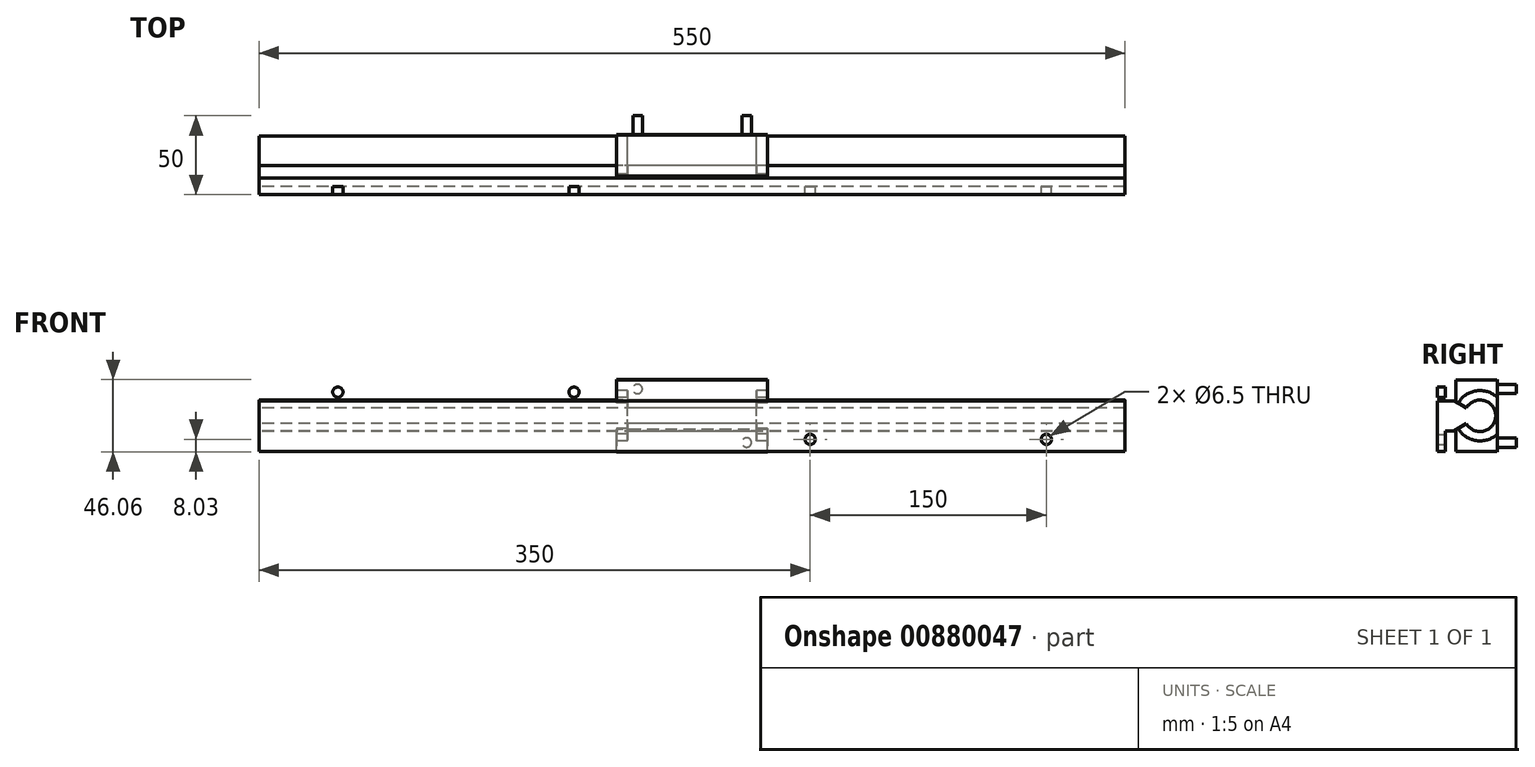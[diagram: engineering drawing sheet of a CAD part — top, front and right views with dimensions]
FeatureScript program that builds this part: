
annotation { "Feature Type Name" : "Feature", "Feature Type Description" : "" }
export const myFeature = defineFeature(function(context is Context, id is Id, definition is map)
    precondition{}
    {
        {
            var Q0;
            Q0=qCreatedBy(makeId("Right.planeOp"),FACE);
            var sketch = newSketch(context, id + "F0", { "sketchPlane" : qUnion([Q0])});
            skLineSegment(sketch, "E0", {"start": v(23, 0) * mm, "end": v(23, -24.18) * mm});
            skLineSegment(sketch, "E1", {"start": v(23, -24.18) * mm, "end": v(12, -24.18) * mm});
            skLineSegment(sketch, "E2", {"start": v(12, -24.18) * mm, "end": v(10.8, -22.8) * mm});
            skLineSegment(sketch, "E3", {"start": v(10.8, -22.8) * mm, "end": v(-15.2, -22.8) * mm});
            skLineSegment(sketch, "E4", {"start": v(-15.2, -22.8) * mm, "end": v(-15.2, -8.78) * mm});
            skArc(sketch, "E5", {"start": v(-8.66, -5) * mm, "mid": v(2.59, -9.66) * mm, "end": v(10, 0) * mm});
            skArc(sketch, "E6.0", {"start": v(-13.86, -8) * mm, "mid": v(4.14, -15.45) * mm, "end": v(16, 0) * mm});
            skLineSegment(sketch, "E7", {"start": v(-8.66, -5) * mm, "end": v(-16.54, -9.55) * mm});
            skPoint(sketch, "E8.orphan", {"position": v(-5, 0) * mm});
            skPoint(sketch, "E9.orphan", {"position": v(-16, 0) * mm});
            skPoint(sketch, "E10.MirrorP", {"position": v(-8, 0) * mm});
            skPoint(sketch, "E11.orphan", {"position": v(-27, 0) * mm});
            skLineSegment(sketch, "E12.top", {"start": v(-27, -22.6) * mm, "end": v(-22, -22.6) * mm});
            skLineSegment(sketch, "E12.left", {"start": v(-27, 0) * mm, "end": v(-27, -22.6) * mm});
            skLineSegment(sketch, "E12.right", {"start": v(-22, -12.7) * mm, "end": v(-22, -22.6) * mm});
            skLineSegment(sketch, "E13.MirrorCS", {"start": v(12, 24.18) * mm, "end": v(10.8, 22.8) * mm});
            skLineSegment(sketch, "E14.MirrorCS", {"start": v(-15.2, 22.8) * mm, "end": v(-15.2, 8.78) * mm});
            skLineSegment(sketch, "E15.MirrorCS", {"start": v(-27, 22.6) * mm, "end": v(-22, 22.6) * mm});
            skLineSegment(sketch, "E16.MirrorCS", {"start": v(-22, 12.7) * mm, "end": v(-22, 22.6) * mm});
            skLineSegment(sketch, "E17.MirrorCS", {"start": v(23, 24.18) * mm, "end": v(12, 24.18) * mm});
            skLineSegment(sketch, "E18.MirrorCS", {"start": v(-8.66, 5) * mm, "end": v(-16.54, 9.55) * mm});
            skLineSegment(sketch, "E19.MirrorCS", {"start": v(10.8, 22.8) * mm, "end": v(-15.2, 22.8) * mm});
            skArc(sketch, "E20.MirrorCS", {"start": v(-13.86, 8) * mm, "mid": v(4.14, 15.45) * mm, "end": v(16, 0) * mm});
            skLineSegment(sketch, "E21.MirrorCS", {"start": v(23, 0) * mm, "end": v(23, 24.18) * mm});
            skLineSegment(sketch, "E22.MirrorCS", {"start": v(-27, 0) * mm, "end": v(-27, 22.6) * mm});
            skArc(sketch, "E23.MirrorCS", {"start": v(-8.66, 5) * mm, "mid": v(2.59, 9.66) * mm, "end": v(10, 0) * mm});
            skLineSegment(sketch, "E24", {"start": v(-16.54, -9.55) * mm, "end": v(-22, -9.55) * mm});
            skLineSegment(sketch, "E25", {"start": v(-22, -12.7) * mm, "end": v(-22, -9.55) * mm});
            skLineSegment(sketch, "E26.MirrorCS", {"start": v(-16.54, 9.55) * mm, "end": v(-22, 9.55) * mm});
            skLineSegment(sketch, "E27.MirrorCS", {"start": v(-22, 12.7) * mm, "end": v(-22, 9.55) * mm});
            skSolve(sketch);
        }
        {
            var Q0;
            Q0=makeQuery(id+"F0.imprint","IMPRINT",FACE,{"disambiguationData":[TD([[makeQuery(id+"F0.imprint","IMPRINT",EDGE,{"derivedFrom":sQuery(id+"F0.wireOp",EDGE,"E0")}),-1.0]])]});
            extrude(context, id + "F1", {"entities" : qUnion([Q0]), "endBound" : BoundingType.SYMMETRIC, "depth" : 96 * mm});
        }
        {
            var Q0;
            Q0=makeQuery(id+"F1.opExtrude","CAP_FACE",FACE,{"disambiguationData":[OSD([sQuery(id+"F0.wireOp",EDGE,"E0"),sQuery(id+"F0.wireOp",EDGE,"E1"),sQuery(id+"F0.wireOp",EDGE,"E2"),sQuery(id+"F0.wireOp",EDGE,"E3"),sQuery(id+"F0.wireOp",EDGE,"E4"),sQuery(id+"F0.wireOp",EDGE,"df6029b9-db81-4ef9-b3c9-fa889dd918b3.trimOffspring"),sQuery(id+"F0.wireOp",EDGE,"E6.0"),sQuery(id+"F0.wireOp",EDGE,"a8d7aa04-359c-4e10-92e7-1a1d4cf787390.MirrorCS"),sQuery(id+"F0.wireOp",EDGE,"a8d7aa04-359c-4e10-92e7-1a1d4cf787391.MirrorCS"),sQuery(id+"F0.wireOp",EDGE,"a8d7aa04-359c-4e10-92e7-1a1d4cf787392.MirrorCS"),sQuery(id+"F0.wireOp",EDGE,"a8d7aa04-359c-4e10-92e7-1a1d4cf787393.MirrorCS"),sQuery(id+"F0.wireOp",EDGE,"a8d7aa04-359c-4e10-92e7-1a1d4cf787394.MirrorCS"),sQuery(id+"F0.wireOp",EDGE,"a8d7aa04-359c-4e10-92e7-1a1d4cf787396.MirrorCS"),sQuery(id+"F0.wireOp",EDGE,"a8d7aa04-359c-4e10-92e7-1a1d4cf787397.MirrorCS")])],"isStart":false});
            cPlane(context, id + "F2", {"entities" : qUnion([Q0]), "cplaneType" : CPlaneType.OFFSET, "offset" : 2 * mm, "oppositeDirection" : true, "width" : 150 * mm, "height" : 150 * mm});
        }
        {
            var Q0;
            Q0=makeQuery(id+"F0.imprint","IMPRINT",FACE,{"disambiguationData":[TD([[makeQuery(id+"F0.imprint","IMPRINT",EDGE,{"derivedFrom":sQuery(id+"F0.wireOp",EDGE,"E5")}),-1.0]])]});
            var Q1;
            Q1=qCreatedBy(id+"F2.planeOp",FACE);
            extrude(context, id + "F3", {"entities" : qUnion([Q0]), "operationType" : NewBodyOperationType.ADD, "endBound" : BoundingType.SYMMETRIC, "endBoundEntityFace" : qUnion([Q1]), "depth" : 82 * mm});
        }
        {
            var Q0;
            {var subQ4=sQuery(id+"F0.wireOp",EDGE,"E5");Q0=makeQuery(id+"F0.imprint","IMPRINT",FACE,{"disambiguationData":[TD([[makeQuery(id+"F0.imprint","IMPRINT",EDGE,{"derivedFrom":subQ4}),1.0]])]});}
            extrude(context, id + "F4", {"entities" : qUnion([Q0]), "endBound" : BoundingType.SYMMETRIC, "depth" : 550 * mm});
        }
        {
            var Q0;
            Q0=makeQuery(id+"F1.opExtrude","SWEPT_FACE",FACE,{"disambiguationData":[OSD([sQuery(id+"F0.wireOp",EDGE,"E0"),sQuery(id+"F0.wireOp",EDGE,"766315b1-5346-49c8-9387-2592a379b26e5.MirrorCS")])]});
            var sketch = newSketch(context, id + "F5", { "sketchPlane" : qUnion([Q0])});
            skCircle(sketch, "E28", {"center": v(-34.62, 17) * mm, "radius": 3 * mm});
            skCircle(sketch, "E29.MirrorC", {"center": v(34.62, 17) * mm, "radius": 3 * mm});
            skCircle(sketch, "E30.MirrorC", {"center": v(-34.62, -17) * mm, "radius": 3 * mm});
            skCircle(sketch, "E31.MirrorC", {"center": v(34.62, -17) * mm, "radius": 3 * mm});
            skSolve(sketch);
        }
        {
            var Q0;
            Q0=makeQuery(id+"F5.imprint","IMPRINT",FACE,{"disambiguationData":[TD([[makeQuery(id+"F5.imprint","IMPRINT",EDGE,{"derivedFrom":sQuery(id+"F5.wireOp",EDGE,"E28")}),1.0]])]});
            var Q1;
            Q1=makeQuery(id+"F5.imprint","IMPRINT",FACE,{"disambiguationData":[TD([[makeQuery(id+"F5.imprint","IMPRINT",EDGE,{"derivedFrom":sQuery(id+"F5.wireOp",EDGE,"E29.MirrorC")}),-1.0]])]});
            var Q2;
            Q2=makeQuery(id+"F5.imprint","IMPRINT",FACE,{"disambiguationData":[TD([[makeQuery(id+"F5.imprint","IMPRINT",EDGE,{"derivedFrom":sQuery(id+"F5.wireOp",EDGE,"E31.MirrorC")}),1.0]])]});
            var Q3;
            Q3=makeQuery(id+"F5.imprint","IMPRINT",FACE,{"disambiguationData":[TD([[makeQuery(id+"F5.imprint","IMPRINT",EDGE,{"derivedFrom":sQuery(id+"F5.wireOp",EDGE,"E30.MirrorC")}),-1.0]])]});
            extrude(context, id + "F6", {"entities" : qUnion([Q0, Q1, Q2, Q3]), "operationType" : NewBodyOperationType.REMOVE, "oppositeDirection" : true, "depth" : 12 * mm});
        }
        {
            var Q0;
            Q0=makeQuery(id+"F4.opExtrude","SWEPT_FACE",FACE,{"disambiguationData":[OSD([sQuery(id+"F0.wireOp",EDGE,"E16.MirrorCS")])]});
            var sketch = newSketch(context, id + "F7", { "sketchPlane" : qUnion([Q0])});
            skCircle(sketch, "E32", {"center": v(-225, 15) * mm, "radius": 3.25 * mm});
            skCircle(sketch, "E33", {"center": v(-225, -15) * mm, "radius": 3.25 * mm});
            skCircle(sketch, "E34.1.0.0", {"center": v(-75, -15) * mm, "radius": 3.25 * mm});
            skCircle(sketch, "E34.1.0.1", {"center": v(-75, 15) * mm, "radius": 3.25 * mm});
            skLineSegment(sketch, "E34.direction1", {"start": v(-225, -15) * mm, "end": v(-75, -15) * mm, "construction": true});
            skCircle(sketch, "E35.MirrorC", {"center": v(75, -15) * mm, "radius": 3.25 * mm});
            skCircle(sketch, "E36.MirrorC", {"center": v(225, -15) * mm, "radius": 3.25 * mm});
            skCircle(sketch, "E37.MirrorC", {"center": v(75, 15) * mm, "radius": 3.25 * mm});
            skCircle(sketch, "E38.MirrorC", {"center": v(225, 15) * mm, "radius": 3.25 * mm});
            skLineSegment(sketch, "E39.MirrorCS", {"start": v(225, -15) * mm, "end": v(75, -15) * mm, "construction": true});
            skSolve(sketch);
        }
        {
            var Q0;
            Q0=makeQuery(id+"F7.imprint","IMPRINT",FACE,{"disambiguationData":[TD([[makeQuery(id+"F7.imprint","IMPRINT",EDGE,{"derivedFrom":sQuery(id+"F7.wireOp",EDGE,"E32")}),1.0]])]});
            var Q1;
            Q1=makeQuery(id+"F7.imprint","IMPRINT",FACE,{"disambiguationData":[TD([[makeQuery(id+"F7.imprint","IMPRINT",EDGE,{"derivedFrom":sQuery(id+"F7.wireOp",EDGE,"E34.1.0.1")}),1.0]])]});
            var Q2;
            Q2=makeQuery(id+"F7.imprint","IMPRINT",FACE,{"disambiguationData":[TD([[makeQuery(id+"F7.imprint","IMPRINT",EDGE,{"derivedFrom":sQuery(id+"F7.wireOp",EDGE,"E33")}),1.0]])]});
            var Q3;
            Q3=makeQuery(id+"F7.imprint","IMPRINT",FACE,{"disambiguationData":[TD([[makeQuery(id+"F7.imprint","IMPRINT",EDGE,{"derivedFrom":sQuery(id+"F7.wireOp",EDGE,"E34.1.0.0")}),1.0]])]});
            var Q4;
            Q4=makeQuery(id+"F7.imprint","IMPRINT",FACE,{"disambiguationData":[TD([[makeQuery(id+"F7.imprint","IMPRINT",EDGE,{"derivedFrom":sQuery(id+"F7.wireOp",EDGE,"E37.MirrorC")}),-1.0]])]});
            var Q5;
            Q5=makeQuery(id+"F7.imprint","IMPRINT",FACE,{"disambiguationData":[TD([[makeQuery(id+"F7.imprint","IMPRINT",EDGE,{"derivedFrom":sQuery(id+"F7.wireOp",EDGE,"E38.MirrorC")}),-1.0]])]});
            var Q6;
            Q6=makeQuery(id+"F7.imprint","IMPRINT",FACE,{"disambiguationData":[TD([[makeQuery(id+"F7.imprint","IMPRINT",EDGE,{"derivedFrom":sQuery(id+"F7.wireOp",EDGE,"E36.MirrorC")}),-1.0]])]});
            var Q7;
            Q7=makeQuery(id+"F7.imprint","IMPRINT",FACE,{"disambiguationData":[TD([[makeQuery(id+"F7.imprint","IMPRINT",EDGE,{"derivedFrom":sQuery(id+"F7.wireOp",EDGE,"E35.MirrorC")}),-1.0]])]});
            extrude(context, id + "F8", {"entities" : qUnion([Q0, Q1, Q2, Q3, Q4, Q5, Q6, Q7]), "operationType" : NewBodyOperationType.REMOVE, "oppositeDirection" : true, "depth" : 25 * mm});
        }
    });
